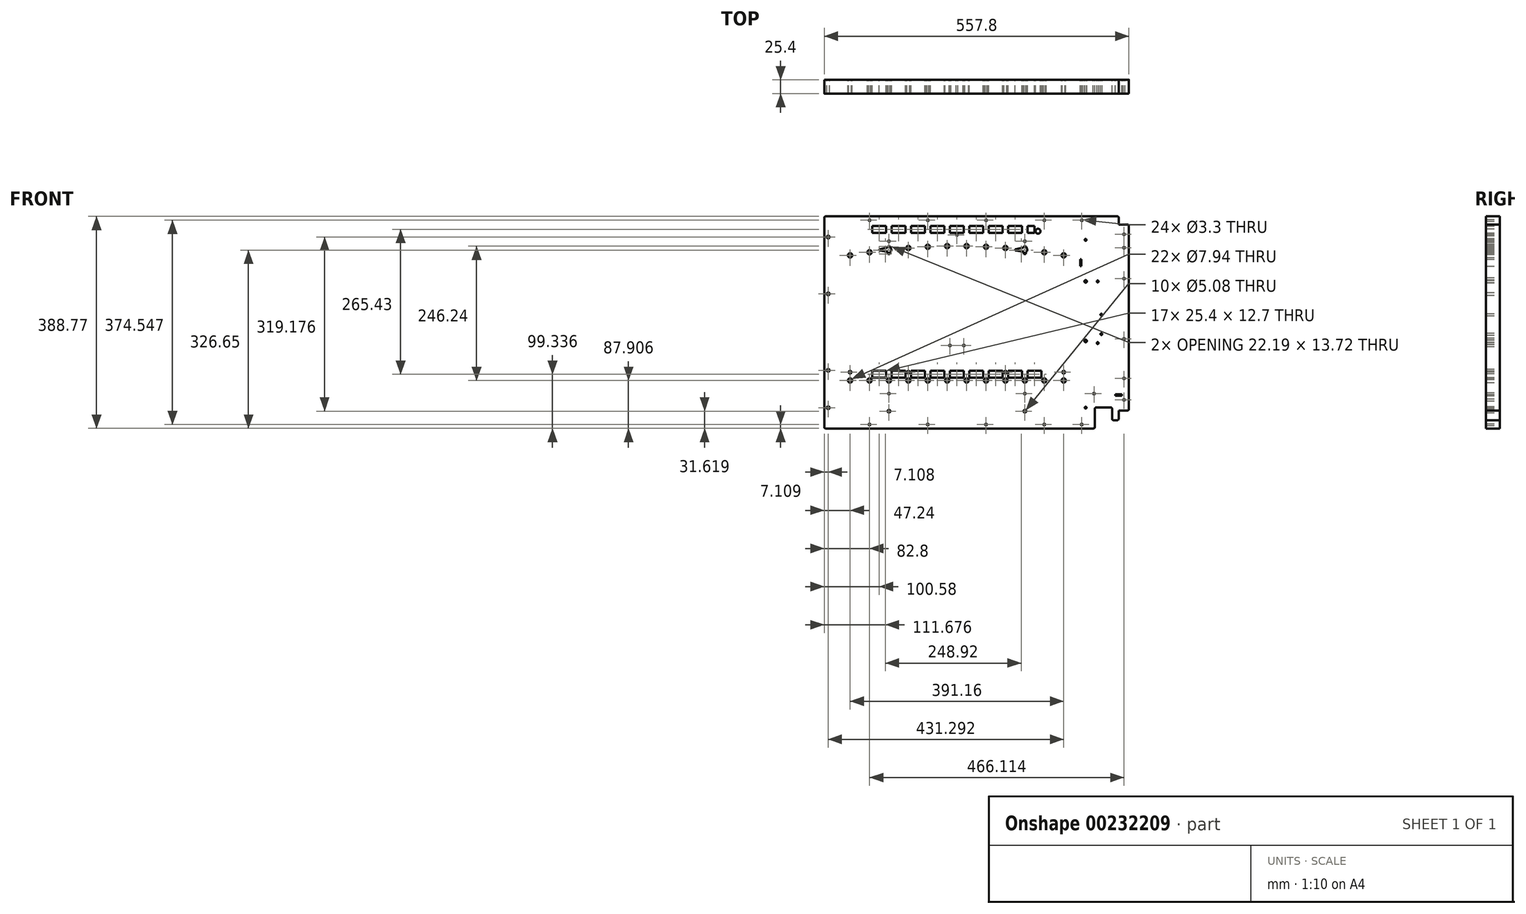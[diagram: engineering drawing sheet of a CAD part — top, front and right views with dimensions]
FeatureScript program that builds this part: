
annotation { "Feature Type Name" : "Feature", "Feature Type Description" : "" }
export const myFeature = defineFeature(function(context is Context, id is Id, definition is map)
    precondition{}
    {
        {
            var Q0;
            Q0=qCreatedBy(makeId("Front.planeOp"),FACE);
            var sketch = newSketch(context, id + "F0", { "sketchPlane" : qUnion([Q0])});
            skCircle(sketch, "E0", {"center": v(270.01, 168.97) * mm, "radius": 1.65 * mm});
            skCircle(sketch, "E1", {"center": v(270.01, 144.35) * mm, "radius": 1.65 * mm});
            skCircle(sketch, "E2", {"center": v(270.01, 87.69) * mm, "radius": 1.65 * mm});
            skCircle(sketch, "E3", {"center": v(270.01, -22.8) * mm, "radius": 1.65 * mm});
            skCircle(sketch, "E4", {"center": v(270.01, -134.56) * mm, "radius": 1.65 * mm});
            skCircle(sketch, "E5", {"center": v(270.01, -95.2) * mm, "radius": 1.65 * mm});
            skCircle(sketch, "E6", {"center": v(-196.1, -179.8) * mm, "radius": 1.65 * mm});
            skCircle(sketch, "E7", {"center": v(-89.42, -179.8) * mm, "radius": 1.65 * mm});
            skCircle(sketch, "E8", {"center": v(17.26, -179.8) * mm, "radius": 1.65 * mm});
            skCircle(sketch, "E9", {"center": v(123.94, -179.8) * mm, "radius": 1.65 * mm});
            skCircle(sketch, "E10", {"center": v(192.52, -179.8) * mm, "radius": 1.65 * mm});
            skCircle(sketch, "E11", {"center": v(-196.1, 194.75) * mm, "radius": 1.65 * mm});
            skCircle(sketch, "E12", {"center": v(-89.42, 194.75) * mm, "radius": 1.65 * mm});
            skCircle(sketch, "E13", {"center": v(17.26, 194.75) * mm, "radius": 1.65 * mm});
            skCircle(sketch, "E14", {"center": v(123.94, 194.75) * mm, "radius": 1.65 * mm});
            skCircle(sketch, "E15", {"center": v(192.52, 194.75) * mm, "radius": 1.65 * mm});
            skCircle(sketch, "E16", {"center": v(-196.1, 136) * mm, "radius": 3.97 * mm});
            skCircle(sketch, "E17", {"center": v(-124.98, 143.87) * mm, "radius": 3.97 * mm});
            skCircle(sketch, "E18", {"center": v(-89.42, 146.12) * mm, "radius": 3.97 * mm});
            skCircle(sketch, "E19", {"center": v(-53.86, 147.24) * mm, "radius": 3.97 * mm});
            skCircle(sketch, "E20", {"center": v(17.26, 146.12) * mm, "radius": 3.97 * mm});
            skCircle(sketch, "E21", {"center": v(-18.3, 147.24) * mm, "radius": 3.97 * mm});
            skCircle(sketch, "E22", {"center": v(52.82, 143.87) * mm, "radius": 3.97 * mm});
            skCircle(sketch, "E23", {"center": v(123.94, 136) * mm, "radius": 3.97 * mm});
            skCircle(sketch, "E24", {"center": v(-196.1, -99) * mm, "radius": 3.97 * mm});
            skCircle(sketch, "E25", {"center": v(-160.54, -99) * mm, "radius": 3.97 * mm});
            skCircle(sketch, "E26", {"center": v(-124.98, -99) * mm, "radius": 3.97 * mm});
            skCircle(sketch, "E27", {"center": v(-89.42, -99) * mm, "radius": 3.97 * mm});
            skCircle(sketch, "E28", {"center": v(-53.86, -99) * mm, "radius": 3.97 * mm});
            skCircle(sketch, "E29", {"center": v(-18.3, -99) * mm, "radius": 3.97 * mm});
            skCircle(sketch, "E30", {"center": v(17.26, -99) * mm, "radius": 3.97 * mm});
            skCircle(sketch, "E31", {"center": v(52.82, -99) * mm, "radius": 3.97 * mm});
            skCircle(sketch, "E32", {"center": v(88.38, -99) * mm, "radius": 3.97 * mm});
            skCircle(sketch, "E33", {"center": v(123.94, -99) * mm, "radius": 3.97 * mm});
            skCircle(sketch, "E34", {"center": v(159.5, 130.33) * mm, "radius": 3.97 * mm});
            skCircle(sketch, "E35", {"center": v(159.5, -99) * mm, "radius": 3.97 * mm});
            skCircle(sketch, "E36", {"center": v(-231.66, -99) * mm, "radius": 3.97 * mm});
            skCircle(sketch, "E37", {"center": v(-231.66, 130.33) * mm, "radius": 3.97 * mm});
            skCircle(sketch, "E38", {"center": v(-271.8, 163.89) * mm, "radius": 2.54 * mm});
            skCircle(sketch, "E39", {"center": v(-271.8, 59.75) * mm, "radius": 2.54 * mm});
            skCircle(sketch, "E40", {"center": v(-271.8, -148.94) * mm, "radius": 2.54 * mm});
            skCircle(sketch, "E41", {"center": v(-160.54, 156.27) * mm, "radius": 1.65 * mm});
            skCircle(sketch, "E42", {"center": v(88.38, 156.27) * mm, "radius": 1.65 * mm});
            skCircle(sketch, "E43", {"center": v(-36.08, 167.95) * mm, "radius": 1.65 * mm});
            skCircle(sketch, "E44", {"center": v(199.63, 82.6) * mm, "radius": 2.29 * mm});
            skCircle(sketch, "E45", {"center": v(221.73, 82.6) * mm, "radius": 1.66 * mm});
            skCircle(sketch, "E46", {"center": v(199.63, -26.61) * mm, "radius": 2.29 * mm});
            skCircle(sketch, "E47", {"center": v(221.73, -30.42) * mm, "radius": 1.66 * mm});
            skCircle(sketch, "E48", {"center": v(-160.54, -155.3) * mm, "radius": 2.54 * mm});
            skCircle(sketch, "E49", {"center": v(88.38, -155.3) * mm, "radius": 2.54 * mm});
            skCircle(sketch, "E50", {"center": v(-231.66, -83.76) * mm, "radius": 2.54 * mm});
            skCircle(sketch, "E51", {"center": v(159.5, -83.76) * mm, "radius": 2.54 * mm});
            skCircle(sketch, "E52", {"center": v(-160.54, -123.13) * mm, "radius": 1.65 * mm});
            skCircle(sketch, "E53", {"center": v(88.38, -123.13) * mm, "radius": 1.65 * mm});
            skCircle(sketch, "E54", {"center": v(-271.8, -80.36) * mm, "radius": 2.54 * mm});
            skCircle(sketch, "E55", {"center": v(-124.98, -83.76) * mm, "radius": 2.54 * mm});
            skCircle(sketch, "E56", {"center": v(52.82, -83.76) * mm, "radius": 2.54 * mm});
            skCircle(sketch, "E57", {"center": v(228.49, -13.91) * mm, "radius": 1.66 * mm});
            skCircle(sketch, "E58", {"center": v(228.49, 21.65) * mm, "radius": 1.66 * mm});
            skCircle(sketch, "E59", {"center": v(112.5, 174.6) * mm, "radius": 4.45 * mm});
            skCircle(sketch, "E60", {"center": v(199.63, 158.8) * mm, "radius": 1.66 * mm});
            skCircle(sketch, "E61", {"center": v(199.63, -148.94) * mm, "radius": 1.66 * mm});
            skCircle(sketch, "E62", {"center": v(-48.78, -34.87) * mm, "radius": 1.65 * mm});
            skCircle(sketch, "E63", {"center": v(-23.38, -34.87) * mm, "radius": 1.65 * mm});
            skCircle(sketch, "E64", {"center": v(214.97, -123.13) * mm, "radius": 1.65 * mm});
            skLineSegment(sketch, "E65", {"start": v(-48.78, 171.5) * mm, "end": v(-23.38, 171.5) * mm});
            skLineSegment(sketch, "E66", {"start": v(-23.38, 171.5) * mm, "end": v(-23.38, 184.2) * mm});
            skLineSegment(sketch, "E67", {"start": v(-23.38, 184.2) * mm, "end": v(-48.78, 184.2) * mm});
            skLineSegment(sketch, "E68", {"start": v(-48.78, 184.2) * mm, "end": v(-48.78, 171.5) * mm});
            skLineSegment(sketch, "E69", {"start": v(-58.94, 184.2) * mm, "end": v(-84.34, 184.2) * mm});
            skLineSegment(sketch, "E70", {"start": v(-84.34, 184.2) * mm, "end": v(-84.34, 171.5) * mm});
            skLineSegment(sketch, "E71", {"start": v(-84.34, 171.5) * mm, "end": v(-58.94, 171.5) * mm});
            skLineSegment(sketch, "E72", {"start": v(-58.94, 171.5) * mm, "end": v(-58.94, 184.2) * mm});
            skLineSegment(sketch, "E73", {"start": v(-94.5, 184.2) * mm, "end": v(-119.9, 184.2) * mm});
            skLineSegment(sketch, "E74", {"start": v(-119.9, 184.2) * mm, "end": v(-119.9, 171.5) * mm});
            skLineSegment(sketch, "E75", {"start": v(-119.9, 171.5) * mm, "end": v(-94.5, 171.5) * mm});
            skLineSegment(sketch, "E76", {"start": v(-94.5, 171.5) * mm, "end": v(-94.5, 184.2) * mm});
            skLineSegment(sketch, "E77", {"start": v(-130.06, 184.2) * mm, "end": v(-155.46, 184.2) * mm});
            skLineSegment(sketch, "E78", {"start": v(-155.46, 184.2) * mm, "end": v(-155.46, 171.5) * mm});
            skLineSegment(sketch, "E79", {"start": v(-155.46, 171.5) * mm, "end": v(-130.06, 171.5) * mm});
            skLineSegment(sketch, "E80", {"start": v(-130.06, 171.5) * mm, "end": v(-130.06, 184.2) * mm});
            skLineSegment(sketch, "E81", {"start": v(-165.62, 184.2) * mm, "end": v(-191.02, 184.2) * mm});
            skLineSegment(sketch, "E82", {"start": v(-191.02, 184.2) * mm, "end": v(-191.02, 171.5) * mm});
            skLineSegment(sketch, "E83", {"start": v(-191.02, 171.5) * mm, "end": v(-165.62, 171.5) * mm});
            skLineSegment(sketch, "E84", {"start": v(-165.62, 171.5) * mm, "end": v(-165.62, 184.2) * mm});
            skLineSegment(sketch, "E85", {"start": v(-13.22, 171.5) * mm, "end": v(12.18, 171.5) * mm});
            skLineSegment(sketch, "E86", {"start": v(12.18, 171.5) * mm, "end": v(12.18, 184.2) * mm});
            skLineSegment(sketch, "E87", {"start": v(12.18, 184.2) * mm, "end": v(-13.22, 184.2) * mm});
            skLineSegment(sketch, "E88", {"start": v(-13.22, 184.2) * mm, "end": v(-13.22, 171.5) * mm});
            skLineSegment(sketch, "E89", {"start": v(22.34, 171.5) * mm, "end": v(47.74, 171.5) * mm});
            skLineSegment(sketch, "E90", {"start": v(47.74, 171.5) * mm, "end": v(47.74, 184.2) * mm});
            skLineSegment(sketch, "E91", {"start": v(47.74, 184.2) * mm, "end": v(22.34, 184.2) * mm});
            skLineSegment(sketch, "E92", {"start": v(22.34, 184.2) * mm, "end": v(22.34, 171.5) * mm});
            skLineSegment(sketch, "E93", {"start": v(57.9, 171.5) * mm, "end": v(83.3, 171.5) * mm});
            skLineSegment(sketch, "E94", {"start": v(83.3, 171.5) * mm, "end": v(83.3, 184.2) * mm});
            skLineSegment(sketch, "E95", {"start": v(83.3, 184.2) * mm, "end": v(57.9, 184.2) * mm});
            skLineSegment(sketch, "E96", {"start": v(57.9, 184.2) * mm, "end": v(57.9, 171.5) * mm});
            skLineSegment(sketch, "E97", {"start": v(93.46, 171.5) * mm, "end": v(106.16, 171.5) * mm});
            skLineSegment(sketch, "E98", {"start": v(106.16, 171.5) * mm, "end": v(106.16, 184.2) * mm});
            skLineSegment(sketch, "E99", {"start": v(106.16, 184.2) * mm, "end": v(93.46, 184.2) * mm});
            skLineSegment(sketch, "E100", {"start": v(93.46, 184.2) * mm, "end": v(93.46, 171.5) * mm});
            skLineSegment(sketch, "E101", {"start": v(-48.78, -93.92) * mm, "end": v(-23.38, -93.92) * mm});
            skLineSegment(sketch, "E102", {"start": v(-23.38, -93.92) * mm, "end": v(-23.38, -81.22) * mm});
            skLineSegment(sketch, "E103", {"start": v(-23.38, -81.22) * mm, "end": v(-48.78, -81.22) * mm});
            skLineSegment(sketch, "E104", {"start": v(-48.78, -81.22) * mm, "end": v(-48.78, -93.92) * mm});
            skLineSegment(sketch, "E105", {"start": v(-58.94, -81.22) * mm, "end": v(-84.34, -81.22) * mm});
            skLineSegment(sketch, "E106", {"start": v(-84.34, -81.22) * mm, "end": v(-84.34, -93.92) * mm});
            skLineSegment(sketch, "E107", {"start": v(-84.34, -93.92) * mm, "end": v(-58.94, -93.92) * mm});
            skLineSegment(sketch, "E108", {"start": v(-58.94, -93.92) * mm, "end": v(-58.94, -81.22) * mm});
            skLineSegment(sketch, "E109", {"start": v(-94.5, -81.22) * mm, "end": v(-119.9, -81.22) * mm});
            skLineSegment(sketch, "E110", {"start": v(-119.9, -81.22) * mm, "end": v(-119.9, -93.92) * mm});
            skLineSegment(sketch, "E111", {"start": v(-119.9, -93.92) * mm, "end": v(-94.5, -93.92) * mm});
            skLineSegment(sketch, "E112", {"start": v(-94.5, -93.92) * mm, "end": v(-94.5, -81.22) * mm});
            skLineSegment(sketch, "E113", {"start": v(-130.06, -81.22) * mm, "end": v(-155.46, -81.22) * mm});
            skLineSegment(sketch, "E114", {"start": v(-155.46, -81.22) * mm, "end": v(-155.46, -93.92) * mm});
            skLineSegment(sketch, "E115", {"start": v(-155.46, -93.92) * mm, "end": v(-130.06, -93.92) * mm});
            skLineSegment(sketch, "E116", {"start": v(-130.06, -93.92) * mm, "end": v(-130.06, -81.22) * mm});
            skLineSegment(sketch, "E117", {"start": v(-165.62, -81.22) * mm, "end": v(-191.02, -81.22) * mm});
            skLineSegment(sketch, "E118", {"start": v(-191.02, -81.22) * mm, "end": v(-191.02, -93.92) * mm});
            skLineSegment(sketch, "E119", {"start": v(-191.02, -93.92) * mm, "end": v(-165.62, -93.92) * mm});
            skLineSegment(sketch, "E120", {"start": v(-165.62, -93.92) * mm, "end": v(-165.62, -81.22) * mm});
            skLineSegment(sketch, "E121", {"start": v(-13.22, -93.92) * mm, "end": v(12.18, -93.92) * mm});
            skLineSegment(sketch, "E122", {"start": v(12.18, -93.92) * mm, "end": v(12.18, -81.22) * mm});
            skLineSegment(sketch, "E123", {"start": v(12.18, -81.22) * mm, "end": v(-13.22, -81.22) * mm});
            skLineSegment(sketch, "E124", {"start": v(-13.22, -81.22) * mm, "end": v(-13.22, -93.92) * mm});
            skLineSegment(sketch, "E125", {"start": v(22.34, -93.92) * mm, "end": v(47.74, -93.92) * mm});
            skLineSegment(sketch, "E126", {"start": v(47.74, -93.92) * mm, "end": v(47.74, -81.22) * mm});
            skLineSegment(sketch, "E127", {"start": v(47.74, -81.22) * mm, "end": v(22.34, -81.22) * mm});
            skLineSegment(sketch, "E128", {"start": v(22.34, -81.22) * mm, "end": v(22.34, -93.92) * mm});
            skLineSegment(sketch, "E129", {"start": v(57.9, -93.92) * mm, "end": v(83.3, -93.92) * mm});
            skLineSegment(sketch, "E130", {"start": v(83.3, -93.92) * mm, "end": v(83.3, -81.22) * mm});
            skLineSegment(sketch, "E131", {"start": v(83.3, -81.22) * mm, "end": v(57.9, -81.22) * mm});
            skLineSegment(sketch, "E132", {"start": v(57.9, -81.22) * mm, "end": v(57.9, -93.92) * mm});
            skLineSegment(sketch, "E133", {"start": v(93.46, -93.92) * mm, "end": v(118.86, -93.92) * mm});
            skLineSegment(sketch, "E134", {"start": v(118.86, -93.92) * mm, "end": v(118.86, -81.22) * mm});
            skLineSegment(sketch, "E135", {"start": v(118.86, -81.22) * mm, "end": v(93.46, -81.22) * mm});
            skLineSegment(sketch, "E136", {"start": v(93.46, -81.22) * mm, "end": v(93.46, -93.92) * mm});
            skLineSegment(sketch, "E137", {"start": v(-163.33, 145.92) * mm, "end": v(-163.33, 144.06) * mm});
            skLineSegment(sketch, "E138", {"start": v(-163.33, 144.06) * mm, "end": v(-165.62, 144.06) * mm});
            skLineSegment(sketch, "E139", {"start": v(-165.62, 144.06) * mm, "end": v(-177.3, 141.75) * mm});
            skLineSegment(sketch, "E140", {"start": v(-177.3, 139.26) * mm, "end": v(-165.62, 136.95) * mm});
            skLineSegment(sketch, "E141", {"start": v(-165.62, 136.95) * mm, "end": v(-163.2, 136.95) * mm});
            skLineSegment(sketch, "E142", {"start": v(-162.32, 136.43) * mm, "end": v(-162.32, 133.1) * mm});
            skLineSegment(sketch, "E143", {"start": v(-158.76, 133.1) * mm, "end": v(-158.76, 136.43) * mm});
            skLineSegment(sketch, "E144", {"start": v(-157.75, 143.96) * mm, "end": v(-157.75, 145.92) * mm});
            skLineSegment(sketch, "E145", {"start": v(85.59, 145.92) * mm, "end": v(85.59, 144.06) * mm});
            skLineSegment(sketch, "E146", {"start": v(85.59, 144.06) * mm, "end": v(83.3, 144.06) * mm});
            skLineSegment(sketch, "E147", {"start": v(83.3, 144.06) * mm, "end": v(71.62, 141.75) * mm});
            skLineSegment(sketch, "E148", {"start": v(71.62, 139.26) * mm, "end": v(83.3, 136.95) * mm});
            skLineSegment(sketch, "E149", {"start": v(83.3, 136.95) * mm, "end": v(85.71, 136.95) * mm});
            skLineSegment(sketch, "E150", {"start": v(86.6, 136.43) * mm, "end": v(86.6, 133.1) * mm});
            skLineSegment(sketch, "E151", {"start": v(90.16, 133.1) * mm, "end": v(90.16, 136.43) * mm});
            skLineSegment(sketch, "E152", {"start": v(91.17, 143.96) * mm, "end": v(91.17, 145.92) * mm});
            skLineSegment(sketch, "E153", {"start": v(189.95, 110.55) * mm, "end": v(191.63, 110.55) * mm});
            skLineSegment(sketch, "E154", {"start": v(191.63, 110.55) * mm, "end": v(191.63, 123.25) * mm});
            skLineSegment(sketch, "E155", {"start": v(191.63, 123.25) * mm, "end": v(189.95, 123.25) * mm});
            skLineSegment(sketch, "E156", {"start": v(189.95, 123.25) * mm, "end": v(189.95, 110.55) * mm});
            skLineSegment(sketch, "E157", {"start": v(253.89, -124.4) * mm, "end": v(253.89, -126.94) * mm});
            skLineSegment(sketch, "E158", {"start": v(253.89, -126.94) * mm, "end": v(266.2, -126.94) * mm});
            skLineSegment(sketch, "E159", {"start": v(266.2, -126.94) * mm, "end": v(266.2, -124.4) * mm});
            skLineSegment(sketch, "E160", {"start": v(266.2, -124.4) * mm, "end": v(253.89, -124.4) * mm});
            skLineSegment(sketch, "E161", {"start": v(278.9, -151.48) * mm, "end": v(278.9, 184.2) * mm});
            skLineSegment(sketch, "E162", {"start": v(260.24, -154.02) * mm, "end": v(276.36, -154.02) * mm});
            skLineSegment(sketch, "E163", {"start": v(260.24, -169.26) * mm, "end": v(260.24, -154.02) * mm});
            skLineSegment(sketch, "E164", {"start": v(250.58, -171.8) * mm, "end": v(257.7, -171.8) * mm});
            skLineSegment(sketch, "E165", {"start": v(248.04, -150.97) * mm, "end": v(248.04, -169.26) * mm});
            skLineSegment(sketch, "E166", {"start": v(219.09, -148.43) * mm, "end": v(245.5, -148.43) * mm});
            skLineSegment(sketch, "E167", {"start": v(216.55, -184.37) * mm, "end": v(216.55, -150.97) * mm});
            skLineSegment(sketch, "E168", {"start": v(-276.36, -186.91) * mm, "end": v(214, -186.91) * mm});
            skLineSegment(sketch, "E169", {"start": v(-278.9, 199.32) * mm, "end": v(-278.9, -184.37) * mm});
            skLineSegment(sketch, "E170", {"start": v(257.7, 201.86) * mm, "end": v(-276.36, 201.86) * mm});
            skLineSegment(sketch, "E171", {"start": v(260.24, 186.75) * mm, "end": v(260.24, 199.32) * mm});
            skLineSegment(sketch, "E172", {"start": v(276.36, 186.75) * mm, "end": v(260.24, 186.75) * mm});
            skArc(sketch, "E173", {"start": v(-177.3, 141.75) * mm, "mid": v(-178.32, 140.5) * mm, "end": v(-177.3, 139.26) * mm});
            skArc(sketch, "E174", {"start": v(-163.2, 136.95) * mm, "mid": v(-162.78, 136.66) * mm, "end": v(-162.32, 136.43) * mm});
            skArc(sketch, "E175", {"start": v(-162.32, 133.1) * mm, "mid": v(-160.54, 132.88) * mm, "end": v(-158.76, 133.1) * mm});
            skArc(sketch, "E176", {"start": v(-158.76, 136.43) * mm, "mid": v(-156.14, 139.9) * mm, "end": v(-157.75, 143.96) * mm});
            skArc(sketch, "E177", {"start": v(-157.75, 145.92) * mm, "mid": v(-160.54, 146.6) * mm, "end": v(-163.33, 145.92) * mm});
            skArc(sketch, "E178", {"start": v(71.62, 141.75) * mm, "mid": v(70.6, 140.5) * mm, "end": v(71.62, 139.26) * mm});
            skArc(sketch, "E179", {"start": v(85.71, 136.95) * mm, "mid": v(86.14, 136.66) * mm, "end": v(86.6, 136.43) * mm});
            skArc(sketch, "E180", {"start": v(86.6, 133.1) * mm, "mid": v(88.38, 132.88) * mm, "end": v(90.16, 133.1) * mm});
            skArc(sketch, "E181", {"start": v(90.16, 136.43) * mm, "mid": v(92.78, 139.9) * mm, "end": v(91.17, 143.96) * mm});
            skArc(sketch, "E182", {"start": v(91.17, 145.92) * mm, "mid": v(88.38, 146.6) * mm, "end": v(85.59, 145.92) * mm});
            skArc(sketch, "E183", {"start": v(276.36, -154.02) * mm, "mid": v(278.16, -153.28) * mm, "end": v(278.9, -151.48) * mm});
            skArc(sketch, "E184", {"start": v(257.7, -171.8) * mm, "mid": v(259.5, -171.06) * mm, "end": v(260.24, -169.26) * mm});
            skArc(sketch, "E185", {"start": v(248.04, -169.26) * mm, "mid": v(248.79, -171.06) * mm, "end": v(250.58, -171.8) * mm});
            skArc(sketch, "E186", {"start": v(248.04, -150.97) * mm, "mid": v(247.3, -149.18) * mm, "end": v(245.5, -148.43) * mm});
            skArc(sketch, "E187", {"start": v(219.09, -148.43) * mm, "mid": v(217.3, -149.18) * mm, "end": v(216.55, -150.97) * mm});
            skArc(sketch, "E188", {"start": v(214, -186.91) * mm, "mid": v(215.8, -186.17) * mm, "end": v(216.55, -184.37) * mm});
            skArc(sketch, "E189", {"start": v(-278.9, -184.37) * mm, "mid": v(-278.16, -186.17) * mm, "end": v(-276.36, -186.91) * mm});
            skArc(sketch, "E190", {"start": v(-276.36, 201.86) * mm, "mid": v(-278.16, 201.11) * mm, "end": v(-278.9, 199.32) * mm});
            skArc(sketch, "E191", {"start": v(260.24, 199.32) * mm, "mid": v(259.5, 201.11) * mm, "end": v(257.7, 201.86) * mm});
            skArc(sketch, "E192", {"start": v(278.9, 184.2) * mm, "mid": v(278.16, 186) * mm, "end": v(276.36, 186.75) * mm});
            skSolve(sketch);
        }
        {
            var Q0;
            Q0 = qSketchRegion(id + "F0", true);
            extrude(context, id + "F1", {"entities" : qUnion([Q0]), "depth" : 25.4 * mm});
        }
    });
